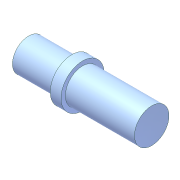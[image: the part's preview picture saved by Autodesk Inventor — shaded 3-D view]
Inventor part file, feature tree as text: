
AUTODESK INVENTOR PART (.ipt)
format: ipt  version: unknown  size: 172,544 bytes
history: native  units: in
note: dims shown in document units (in); Inventor stores cm internally (conversion verified against a paired STEP export)
features: revolve x1, sketch x1
ambient origin geometry x8: Origin, YZ Plane, XZ Plane, XY Plane, X Axis, Y Axis, Z Axis, Center Point
feature tree (2):
  revolve  "Revolution4"  [1 undecoded]
  sketch  "Sketch8"  dims[d2=0.2756in d55=0.2953in d56=0.3937in d57=0.315in d58=0.2756in d59=0.7874in d60=0.1969in d61=0.0in d62=1.2598in d63=90.0deg]
note: 1 required parameter value undecoded (feature->parameter linkage not recoverable at this tier; creation-order binding heuristic only, values carry confidence <= 0.55)
